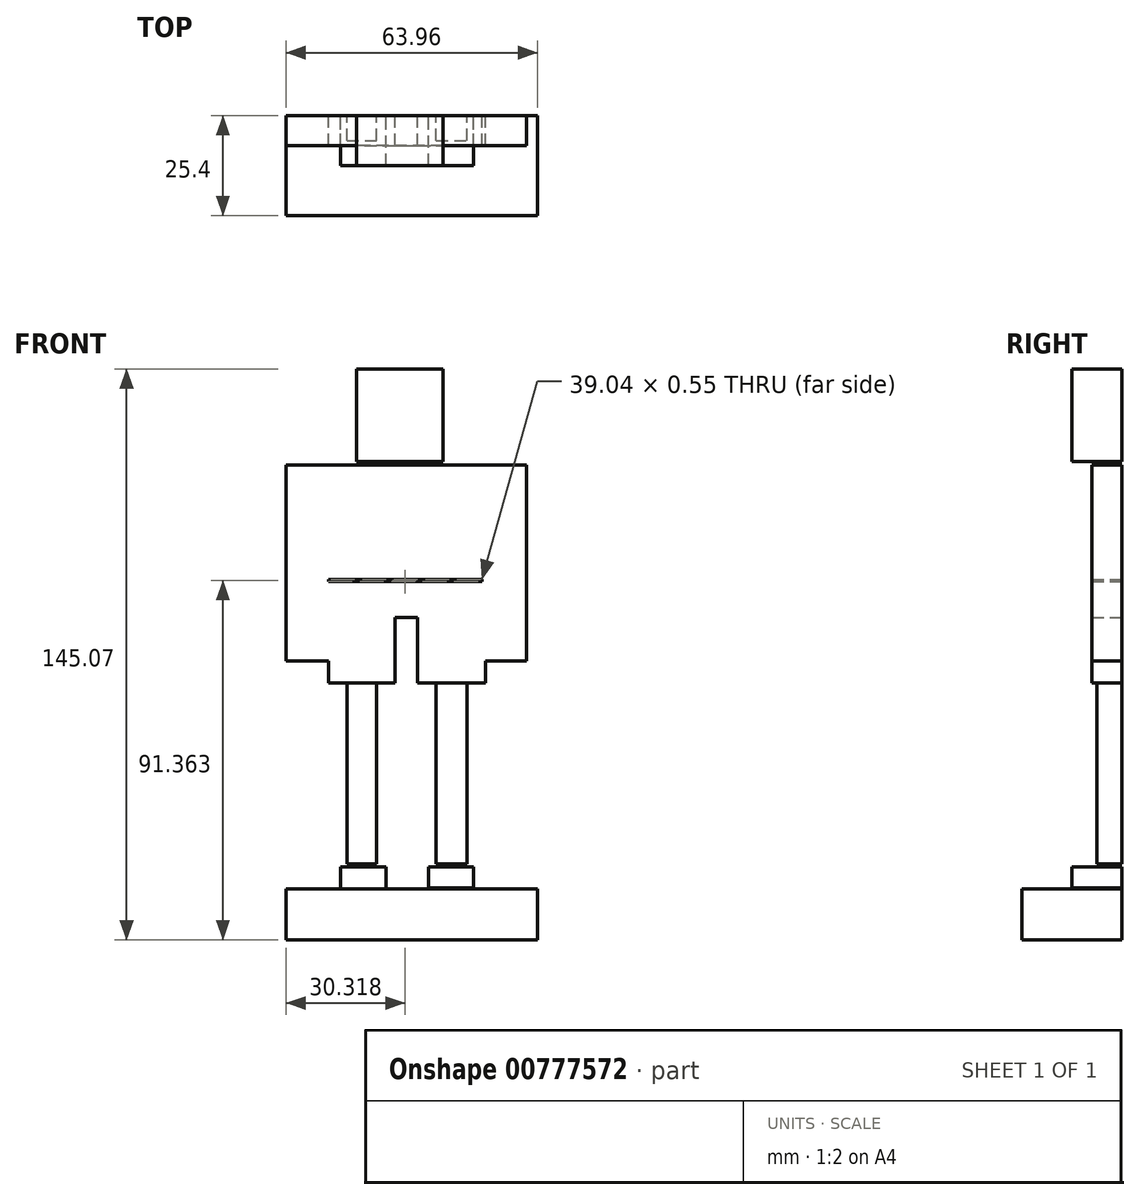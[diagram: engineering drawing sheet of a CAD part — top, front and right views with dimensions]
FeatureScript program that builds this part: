
annotation { "Feature Type Name" : "Feature", "Feature Type Description" : "" }
export const myFeature = defineFeature(function(context is Context, id is Id, definition is map)
    precondition{}
    {
        {
            var Q0;
            Q0=qCreatedBy(makeId("Front.planeOp"),FACE);
            var sketch = newSketch(context, id + "F0", { "sketchPlane" : qUnion([Q0])});
            skLineSegment(sketch, "E0.bottom", {"start": v(-61.11, -52.26) * mm, "end": v(-49.49, -52.26) * mm});
            skLineSegment(sketch, "E0.top", {"start": v(-61.11, -46.72) * mm, "end": v(-49.49, -46.72) * mm});
            skLineSegment(sketch, "E0.left", {"start": v(-61.11, -52.26) * mm, "end": v(-61.11, -46.72) * mm});
            skLineSegment(sketch, "E0.right", {"start": v(-49.49, -52.26) * mm, "end": v(-49.49, -46.72) * mm});
            skLineSegment(sketch, "E1.bottom", {"start": v(-38.69, -46.72) * mm, "end": v(-27.34, -46.72) * mm});
            skLineSegment(sketch, "E1.top", {"start": v(-38.69, -51.98) * mm, "end": v(-27.34, -51.98) * mm});
            skLineSegment(sketch, "E1.left", {"start": v(-38.69, -46.72) * mm, "end": v(-38.69, -51.98) * mm});
            skLineSegment(sketch, "E1.right", {"start": v(-27.34, -46.72) * mm, "end": v(-27.34, -51.98) * mm});
            skSolve(sketch);
        }
        {
            var Q0;
            Q0 = qSketchRegion(id + "F0", true);
            extrude(context, id + "F1", {"entities" : qUnion([Q0]), "depth" : 12.7 * mm, "offsetDistance" : 25.4 * mm});
        }
        {
            var Q0;
            Q0=qCreatedBy(makeId("Front.planeOp"),FACE);
            var sketch = newSketch(context, id + "F2", { "sketchPlane" : qUnion([Q0])});
            skLineSegment(sketch, "E2.bottom", {"start": v(-74.96, -52.26) * mm, "end": v(-11, -52.26) * mm});
            skLineSegment(sketch, "E2.top", {"start": v(-74.96, -65.27) * mm, "end": v(-11, -65.27) * mm});
            skLineSegment(sketch, "E2.left", {"start": v(-74.96, -52.26) * mm, "end": v(-74.96, -65.27) * mm});
            skLineSegment(sketch, "E2.right", {"start": v(-11, -52.26) * mm, "end": v(-11, -65.27) * mm});
            skSolve(sketch);
        }
        {
            var Q0;
            Q0 = qSketchRegion(id + "F2", true);
            extrude(context, id + "F3", {"entities" : qUnion([Q0]), "operationType" : NewBodyOperationType.ADD, "depth" : 25.4 * mm, "offsetDistance" : 25.4 * mm});
        }
        {
            var Q0;
            Q0=qCreatedBy(makeId("Front.planeOp"),FACE);
            var sketch = newSketch(context, id + "F4", { "sketchPlane" : qUnion([Q0])});
            skLineSegment(sketch, "E3.bottom", {"start": v(-74.68, -64.71) * mm, "end": v(-11, -64.71) * mm});
            skLineSegment(sketch, "E3.top", {"start": v(-74.68, -52.53) * mm, "end": v(-11, -52.53) * mm});
            skLineSegment(sketch, "E3.left", {"start": v(-74.68, -64.71) * mm, "end": v(-74.68, -52.53) * mm});
            skLineSegment(sketch, "E3.right", {"start": v(-11, -64.71) * mm, "end": v(-11, -52.53) * mm});
            skSolve(sketch);
        }
        {
            var Q0;
            Q0 = qSketchRegion(id + "F4", true);
            extrude(context, id + "F5", {"entities" : qUnion([Q0]), "operationType" : NewBodyOperationType.ADD, "depth" : 25.4 * mm, "offsetDistance" : 25.4 * mm});
        }
        {
            var Q0;
            Q0=qCreatedBy(makeId("Front.planeOp"),FACE);
            var sketch = newSketch(context, id + "F6", { "sketchPlane" : qUnion([Q0])});
            skLineSegment(sketch, "E4.bottom", {"start": v(-59.45, -45.89) * mm, "end": v(-51.98, -45.89) * mm});
            skLineSegment(sketch, "E4.top", {"start": v(-59.45, 0) * mm, "end": v(-51.98, 0) * mm});
            skLineSegment(sketch, "E4.left", {"start": v(-59.45, -45.89) * mm, "end": v(-59.45, 0) * mm});
            skLineSegment(sketch, "E4.right", {"start": v(-51.98, -45.89) * mm, "end": v(-51.98, 0) * mm});
            skLineSegment(sketch, "E5.bottom", {"start": v(-36.75, -45.89) * mm, "end": v(-29, -45.89) * mm});
            skLineSegment(sketch, "E5.top", {"start": v(-36.75, 0) * mm, "end": v(-29, 0) * mm});
            skLineSegment(sketch, "E5.left", {"start": v(-36.75, -45.89) * mm, "end": v(-36.75, 0) * mm});
            skLineSegment(sketch, "E5.right", {"start": v(-29, -45.89) * mm, "end": v(-29, 0) * mm});
            skSolve(sketch);
        }
        {
            var Q0;
            Q0 = qSketchRegion(id + "F6", true);
            extrude(context, id + "F7", {"entities" : qUnion([Q0]), "depth" : 6.35 * mm, "offsetDistance" : 25.4 * mm});
        }
        {
            var Q0;
            Q0=qCreatedBy(makeId("Front.planeOp"),FACE);
            var sketch = newSketch(context, id + "F8", { "sketchPlane" : qUnion([Q0])});
            skLineSegment(sketch, "E6.bottom", {"start": v(-64.16, 0) * mm, "end": v(-47.27, 0) * mm});
            skLineSegment(sketch, "E6.top", {"start": v(-64.16, 16.68) * mm, "end": v(-47.27, 16.68) * mm});
            skLineSegment(sketch, "E6.left", {"start": v(-64.16, 0) * mm, "end": v(-64.16, 16.68) * mm});
            skLineSegment(sketch, "E6.right", {"start": v(-47.27, 0) * mm, "end": v(-47.27, 16.68) * mm});
            skLineSegment(sketch, "E7.bottom", {"start": v(-41.46, 0) * mm, "end": v(-24.3, 0) * mm});
            skLineSegment(sketch, "E7.top", {"start": v(-41.46, 16.68) * mm, "end": v(-24.3, 16.68) * mm});
            skLineSegment(sketch, "E7.left", {"start": v(-41.46, 0) * mm, "end": v(-41.46, 16.68) * mm});
            skLineSegment(sketch, "E7.right", {"start": v(-24.3, 0) * mm, "end": v(-24.3, 16.68) * mm});
            skLineSegment(sketch, "E8.bottom", {"start": v(-64.16, 16.68) * mm, "end": v(-24.3, 16.68) * mm});
            skLineSegment(sketch, "E8.top", {"start": v(-64.16, 25.82) * mm, "end": v(-24.3, 25.82) * mm});
            skLineSegment(sketch, "E8.left", {"start": v(-64.16, 16.68) * mm, "end": v(-64.16, 25.82) * mm});
            skLineSegment(sketch, "E8.right", {"start": v(-24.3, 16.68) * mm, "end": v(-24.3, 25.82) * mm});
            skSolve(sketch);
        }
        {
            var Q0;
            Q0 = qSketchRegion(id + "F8", true);
            extrude(context, id + "F9", {"entities" : qUnion([Q0]), "depth" : 7.62 * mm, "offsetDistance" : 25.4 * mm});
        }
        {
            var Q0;
            Q0=qCreatedBy(makeId("Front.planeOp"),FACE);
            var sketch = newSketch(context, id + "F10", { "sketchPlane" : qUnion([Q0])});
            skLineSegment(sketch, "E9.bottom", {"start": v(-64.16, 26.37) * mm, "end": v(-25.12, 26.37) * mm});
            skLineSegment(sketch, "E9.top", {"start": v(-64.16, 55.44) * mm, "end": v(-25.12, 55.44) * mm});
            skLineSegment(sketch, "E9.left", {"start": v(-64.16, 26.37) * mm, "end": v(-64.16, 55.44) * mm});
            skLineSegment(sketch, "E9.right", {"start": v(-25.12, 26.37) * mm, "end": v(-25.12, 55.44) * mm});
            skLineSegment(sketch, "E10.bottom", {"start": v(-25.12, 55.44) * mm, "end": v(-13.77, 55.44) * mm});
            skLineSegment(sketch, "E10.top", {"start": v(-25.12, 5.6) * mm, "end": v(-13.77, 5.6) * mm});
            skLineSegment(sketch, "E10.left", {"start": v(-25.12, 55.44) * mm, "end": v(-25.12, 5.6) * mm});
            skLineSegment(sketch, "E10.right", {"start": v(-13.77, 55.44) * mm, "end": v(-13.77, 5.6) * mm});
            skLineSegment(sketch, "E11.bottom", {"start": v(-64.16, 55.44) * mm, "end": v(-74.96, 55.44) * mm});
            skLineSegment(sketch, "E11.top", {"start": v(-64.16, 5.6) * mm, "end": v(-74.96, 5.6) * mm});
            skLineSegment(sketch, "E11.left", {"start": v(-64.16, 55.44) * mm, "end": v(-64.16, 5.6) * mm});
            skLineSegment(sketch, "E11.right", {"start": v(-74.96, 55.44) * mm, "end": v(-74.96, 5.6) * mm});
            skSolve(sketch);
        }
        {
            var Q0;
            Q0 = qSketchRegion(id + "F10", true);
            extrude(context, id + "F11", {"entities" : qUnion([Q0]), "operationType" : NewBodyOperationType.ADD, "depth" : 7.62 * mm, "offsetDistance" : 25.4 * mm});
        }
        {
            var Q0;
            Q0=qCreatedBy(makeId("Front.planeOp"),FACE);
            var sketch = newSketch(context, id + "F12", { "sketchPlane" : qUnion([Q0])});
            skLineSegment(sketch, "E12.bottom", {"start": v(-56.96, 56.27) * mm, "end": v(-35.1, 56.27) * mm});
            skLineSegment(sketch, "E12.top", {"start": v(-56.96, 79.8) * mm, "end": v(-35.1, 79.8) * mm});
            skLineSegment(sketch, "E12.left", {"start": v(-56.96, 56.27) * mm, "end": v(-56.96, 79.8) * mm});
            skLineSegment(sketch, "E12.right", {"start": v(-35.1, 56.27) * mm, "end": v(-35.1, 79.8) * mm});
            skSolve(sketch);
        }
        {
            var Q0;
            Q0 = qSketchRegion(id + "F12", true);
            extrude(context, id + "F13", {"entities" : qUnion([Q0]), "depth" : 12.7 * mm, "offsetDistance" : 25.4 * mm});
        }
        {
            var Q0;
            Q0=qCreatedBy(makeId("Front.planeOp"),FACE);
            var sketch = newSketch(context, id + "F14", { "sketchPlane" : qUnion([Q0])});
            skLineSegment(sketch, "E13.bottom", {"start": v(-53.09, 73.99) * mm, "end": v(-50.6, 73.99) * mm});
            skLineSegment(sketch, "E13.top", {"start": v(-53.09, 70.94) * mm, "end": v(-50.6, 70.94) * mm});
            skLineSegment(sketch, "E13.left", {"start": v(-53.09, 73.99) * mm, "end": v(-53.09, 70.94) * mm});
            skLineSegment(sketch, "E13.right", {"start": v(-50.6, 73.99) * mm, "end": v(-50.6, 70.94) * mm});
            skLineSegment(sketch, "E14.bottom", {"start": v(-46.16, 73.43) * mm, "end": v(-43.4, 73.43) * mm});
            skLineSegment(sketch, "E14.top", {"start": v(-46.16, 70.94) * mm, "end": v(-43.4, 70.94) * mm});
            skLineSegment(sketch, "E14.left", {"start": v(-46.16, 73.43) * mm, "end": v(-46.16, 70.94) * mm});
            skLineSegment(sketch, "E14.right", {"start": v(-43.4, 73.43) * mm, "end": v(-43.4, 70.94) * mm});
            skLineSegment(sketch, "E15.bottom", {"start": v(-50.6, 64.85) * mm, "end": v(-43.4, 64.85) * mm});
            skLineSegment(sketch, "E15.top", {"start": v(-50.6, 62.08) * mm, "end": v(-43.4, 62.08) * mm});
            skLineSegment(sketch, "E15.left", {"start": v(-50.6, 64.85) * mm, "end": v(-50.6, 62.08) * mm});
            skLineSegment(sketch, "E15.right", {"start": v(-43.4, 64.85) * mm, "end": v(-43.4, 62.08) * mm});
            skSolve(sketch);
        }
        {
            var Q0;
            Q0 = qSketchRegion(id + "F14", true);
            extrude(context, id + "F15", {"entities" : qUnion([Q0]), "operationType" : NewBodyOperationType.ADD, "depth" : 6.35 * mm, "offsetDistance" : 25.4 * mm});
        }
    });
